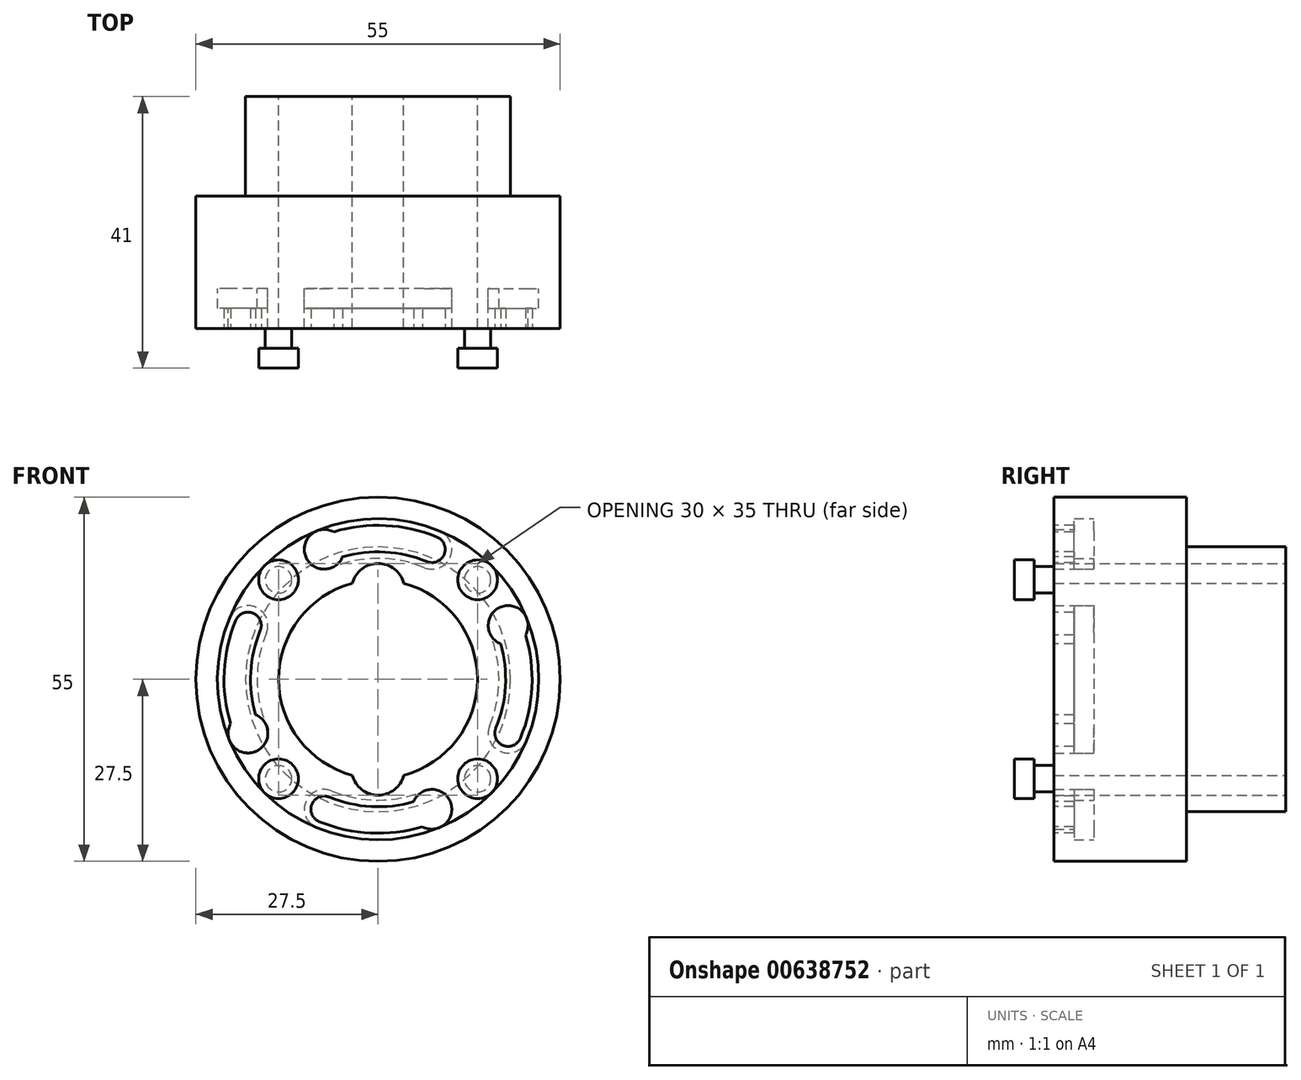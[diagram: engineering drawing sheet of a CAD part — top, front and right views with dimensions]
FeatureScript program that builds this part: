
annotation { "Feature Type Name" : "Feature", "Feature Type Description" : "" }
export const myFeature = defineFeature(function(context is Context, id is Id, definition is map)
    precondition{}
    {
        {
            var Q0;
            Q0=qCreatedBy(makeId("Front.planeOp"),FACE);
            var sketch = newSketch(context, id + "F0", { "sketchPlane" : qUnion([Q0])});
            skCircle(sketch, "E0", {"center": v(0, 0) * mm, "radius": 15 * mm});
            skCircle(sketch, "E1", {"center": v(0, 0) * mm, "radius": 20 * mm});
            skLineSegment(sketch, "E2", {"start": v(-4, 13.5) * mm, "end": v(4, 13.5) * mm});
            skArc(sketch, "E3", {"start": v(4, 13.5) * mm, "mid": v(0, 17.5) * mm, "end": v(-4, 13.5) * mm});
            skArc(sketch, "E4.MirrorCS", {"start": v(4, -13.5) * mm, "mid": v(0, -17.5) * mm, "end": v(-4, -13.5) * mm});
            skLineSegment(sketch, "E5.MirrorCS", {"start": v(-4, -13.5) * mm, "end": v(4, -13.5) * mm});
            skSolve(sketch);
        }
        {
            var Q0;
            Q0=qSketchRegion(id+"F0",true);
            extrude(context, id + "F1", {"entities" : qUnion([Q0]), "depth" : 35 * mm, "offsetDistance" : 25 * mm});
        }
        {
            var Q0;
            Q0=makeQuery(id+"F1.opExtrude","CAP_FACE",FACE,{"disambiguationData":[OSD([sQuery(id+"F0.wireOp",EDGE,"E0"),sQuery(id+"F0.wireOp",EDGE,"E1"),sQuery(id+"F0.wireOp",EDGE,"E3"),sQuery(id+"F0.wireOp",EDGE,"E4.MirrorCS")])],"isStart":false});
            var sketch = newSketch(context, id + "F2", { "sketchPlane" : qUnion([Q0])});
            skCircle(sketch, "E6", {"center": v(0, 0) * mm, "radius": 27.5 * mm});
            skCircle(sketch, "E7", {"center": v(0, 0) * mm, "radius": 20 * mm});
            skSolve(sketch);
        }
        {
            var Q0;
            Q0=qSketchRegion(id+"F2",true);
            extrude(context, id + "F3", {"entities" : qUnion([Q0]), "operationType" : NewBodyOperationType.ADD, "oppositeDirection" : true, "depth" : 20 * mm, "offsetDistance" : 25 * mm});
        }
        {
            var Q0;
            Q0=makeQuery(id+"F3.boolean.opBoolean","MERGE",FACE,{"derivedFrom":[makeQuery(id+"F1.opExtrude","CAP_FACE",FACE,{"disambiguationData":[OSD([sQuery(id+"F0.wireOp",EDGE,"E0"),sQuery(id+"F0.wireOp",EDGE,"E1"),sQuery(id+"F0.wireOp",EDGE,"E3"),sQuery(id+"F0.wireOp",EDGE,"E4.MirrorCS")])],"isStart":false}),makeQuery(id+"F3.opExtrude","CAP_FACE",FACE,{"disambiguationData":[OSD([sQuery(id+"F2.wireOp",EDGE,"E6"),sQuery(id+"F2.wireOp",EDGE,"E7")])],"isStart":true})]});
            var sketch = newSketch(context, id + "F4", { "sketchPlane" : qUnion([Q0])});
            skLineSegment(sketch, "E8", {"start": v(0, 0) * mm, "end": v(15.03, 15.03) * mm, "construction": true});
            skCircle(sketch, "E9", {"center": v(15.03, 15.03) * mm, "radius": 2 * mm});
            skLineSegment(sketch, "E10", {"start": v(0, 0) * mm, "end": v(0, 25.2) * mm, "construction": true});
            skPoint(sketch, "E10.endSnap0", {"position": v(0, 17.5) * mm});
            skCircle(sketch, "E11.1.0", {"center": v(-15.03, 15.03) * mm, "radius": 2 * mm});
            skCircle(sketch, "E11.2.0", {"center": v(-15.03, -15.03) * mm, "radius": 2 * mm});
            skCircle(sketch, "E11.3.0", {"center": v(15.03, -15.03) * mm, "radius": 2 * mm});
            skPoint(sketch, "E11.center", {"position": v(0, 0) * mm});
            skSolve(sketch);
        }
        {
            var Q0;
            Q0 = qSketchRegion(id + "F4", true);
            extrude(context, id + "F5", {"entities" : qUnion([Q0]), "operationType" : NewBodyOperationType.ADD, "depth" : 3 * mm, "offsetDistance" : 25 * mm});
        }
        {
            var Q0;
            Q0=makeQuery(id+"F5.opExtrude","CAP_FACE",FACE,{"disambiguationData":[OSD([sQuery(id+"F4.wireOp",EDGE,"E9")])],"isStart":false});
            var sketch = newSketch(context, id + "F6", { "sketchPlane" : qUnion([Q0])});
            skCircle(sketch, "E12", {"center": v(15.03, 15.03) * mm, "radius": 3 * mm});
            skCircle(sketch, "E13.1.0", {"center": v(-15.03, 15.03) * mm, "radius": 3 * mm});
            skCircle(sketch, "E13.2.0", {"center": v(-15.03, -15.03) * mm, "radius": 3 * mm});
            skCircle(sketch, "E13.3.0", {"center": v(15.03, -15.03) * mm, "radius": 3 * mm});
            skPoint(sketch, "E13.center", {"position": v(0, 0) * mm});
            skSolve(sketch);
        }
        {
            var Q0;
            Q0 = qSketchRegion(id + "F6", true);
            extrude(context, id + "F7", {"entities" : qUnion([Q0]), "operationType" : NewBodyOperationType.ADD, "depth" : 3 * mm, "offsetDistance" : 25 * mm});
        }
        {
            var Q0;
            Q0=makeQuery(id+"F3.boolean.opBoolean","MERGE",FACE,{"derivedFrom":[makeQuery(id+"F1.opExtrude","CAP_FACE",FACE,{"disambiguationData":[OSD([sQuery(id+"F0.wireOp",EDGE,"E0"),sQuery(id+"F0.wireOp",EDGE,"E1"),sQuery(id+"F0.wireOp",EDGE,"E3"),sQuery(id+"F0.wireOp",EDGE,"E4.MirrorCS")])],"isStart":false}),makeQuery(id+"F3.opExtrude","CAP_FACE",FACE,{"disambiguationData":[OSD([sQuery(id+"F2.wireOp",EDGE,"E6"),sQuery(id+"F2.wireOp",EDGE,"E7")])],"isStart":true})]});
            var sketch = newSketch(context, id + "F8", { "sketchPlane" : qUnion([Q0])});
            skLineSegment(sketch, "E14", {"start": v(0, 0) * mm, "end": v(0, 21.25) * mm, "construction": true});
            skLineSegment(sketch, "E15", {"start": v(0, 0) * mm, "end": v(-8.13, 19.63) * mm, "construction": true});
            skLineSegment(sketch, "E16.MirrorCS", {"start": v(0, 0) * mm, "end": v(8.13, 19.63) * mm, "construction": true});
            skCircle(sketch, "E17", {"center": v(-8.13, 19.63) * mm, "radius": 2 * mm});
            skCircle(sketch, "E18.MirrorC", {"center": v(8.13, 19.63) * mm, "radius": 2 * mm});
            skArc(sketch, "E19", {"start": v(-8.91, 21.47) * mm, "mid": v(-4.54, 22.8) * mm, "end": v(0, 23.25) * mm});
            skArc(sketch, "E20", {"start": v(-7.37, 17.78) * mm, "mid": v(-3.76, 18.88) * mm, "end": v(0, 19.25) * mm});
            skArc(sketch, "E21.MirrorCS", {"start": v(8.91, 21.47) * mm, "mid": v(4.54, 22.8) * mm, "end": v(0, 23.25) * mm});
            skArc(sketch, "E22.MirrorCS", {"start": v(7.37, 17.78) * mm, "mid": v(3.76, 18.88) * mm, "end": v(0, 19.25) * mm});
            skLineSegment(sketch, "E23.1.0", {"start": v(0, 0) * mm, "end": v(-21.25, 0) * mm, "construction": true});
            skArc(sketch, "E23.1.1", {"start": v(-21.47, 8.91) * mm, "mid": v(-22.8, 4.54) * mm, "end": v(-23.25, 0) * mm});
            skArc(sketch, "E23.1.2", {"start": v(-17.78, -7.37) * mm, "mid": v(-18.88, -3.76) * mm, "end": v(-19.25, 0) * mm});
            skLineSegment(sketch, "E23.1.3", {"start": v(0, 0) * mm, "end": v(-19.63, 8.13) * mm, "construction": true});
            skArc(sketch, "E23.1.4", {"start": v(-17.78, 7.37) * mm, "mid": v(-18.88, 3.76) * mm, "end": v(-19.25, 0) * mm});
            skLineSegment(sketch, "E23.1.5", {"start": v(0, 0) * mm, "end": v(-19.63, -8.13) * mm, "construction": true});
            skCircle(sketch, "E23.1.6", {"center": v(-19.63, 8.13) * mm, "radius": 2 * mm});
            skArc(sketch, "E23.1.7", {"start": v(-21.47, -8.91) * mm, "mid": v(-22.8, -4.54) * mm, "end": v(-23.25, 0) * mm});
            skCircle(sketch, "E23.1.8", {"center": v(-19.63, -8.13) * mm, "radius": 2 * mm});
            skLineSegment(sketch, "E23.2.0", {"start": v(0, 0) * mm, "end": v(0, -21.25) * mm, "construction": true});
            skArc(sketch, "E23.2.1", {"start": v(-8.91, -21.47) * mm, "mid": v(-4.54, -22.8) * mm, "end": v(0, -23.25) * mm});
            skArc(sketch, "E23.2.2", {"start": v(7.37, -17.78) * mm, "mid": v(3.76, -18.88) * mm, "end": v(0, -19.25) * mm});
            skLineSegment(sketch, "E23.2.3", {"start": v(0, 0) * mm, "end": v(-8.13, -19.63) * mm, "construction": true});
            skArc(sketch, "E23.2.4", {"start": v(-7.37, -17.78) * mm, "mid": v(-3.76, -18.88) * mm, "end": v(0, -19.25) * mm});
            skLineSegment(sketch, "E23.2.5", {"start": v(0, 0) * mm, "end": v(8.13, -19.63) * mm, "construction": true});
            skCircle(sketch, "E23.2.6", {"center": v(-8.13, -19.63) * mm, "radius": 2 * mm});
            skArc(sketch, "E23.2.7", {"start": v(8.91, -21.47) * mm, "mid": v(4.54, -22.8) * mm, "end": v(0, -23.25) * mm});
            skCircle(sketch, "E23.2.8", {"center": v(8.13, -19.63) * mm, "radius": 2 * mm});
            skLineSegment(sketch, "E23.3.0", {"start": v(0, 0) * mm, "end": v(21.25, 0) * mm, "construction": true});
            skArc(sketch, "E23.3.1", {"start": v(21.47, -8.91) * mm, "mid": v(22.8, -4.54) * mm, "end": v(23.25, 0) * mm});
            skArc(sketch, "E23.3.2", {"start": v(17.78, 7.37) * mm, "mid": v(18.88, 3.76) * mm, "end": v(19.25, 0) * mm});
            skLineSegment(sketch, "E23.3.3", {"start": v(0, 0) * mm, "end": v(19.63, -8.13) * mm, "construction": true});
            skArc(sketch, "E23.3.4", {"start": v(17.78, -7.37) * mm, "mid": v(18.88, -3.76) * mm, "end": v(19.25, 0) * mm});
            skLineSegment(sketch, "E23.3.5", {"start": v(0, 0) * mm, "end": v(19.63, 8.13) * mm, "construction": true});
            skCircle(sketch, "E23.3.6", {"center": v(19.63, -8.13) * mm, "radius": 2 * mm});
            skArc(sketch, "E23.3.7", {"start": v(21.47, 8.91) * mm, "mid": v(22.8, 4.54) * mm, "end": v(23.25, 0) * mm});
            skCircle(sketch, "E23.3.8", {"center": v(19.63, 8.13) * mm, "radius": 2 * mm});
            skSolve(sketch);
        }
        {
            var Q0;
            Q0 = qSketchRegion(id + "F8", true);
            extrude(context, id + "F9", {"entities" : qUnion([Q0]), "operationType" : NewBodyOperationType.REMOVE, "oppositeDirection" : true, "depth" : 6 * mm, "offsetDistance" : 25 * mm});
        }
        {
            var Q0;
            Q0=makeQuery(id+"F9.boolean.opBoolean","COPY",FACE,{"derivedFrom":makeQuery(id+"F9.opExtrude","CAP_FACE",FACE,{"disambiguationData":[OSD([sQuery(id+"F8.wireOp",EDGE,"E17"),sQuery(id+"F8.wireOp",EDGE,"E18.MirrorC"),sQuery(id+"F8.wireOp",EDGE,"E19"),sQuery(id+"F8.wireOp",EDGE,"E20"),sQuery(id+"F8.wireOp",EDGE,"E21.MirrorCS"),sQuery(id+"F8.wireOp",EDGE,"E22.MirrorCS")])],"isStart":false})});
            var sketch = newSketch(context, id + "F10", { "sketchPlane" : qUnion([Q0])});
            skLineSegment(sketch, "E24", {"start": v(0, 0) * mm, "end": v(0, 21.25) * mm, "construction": true});
            skLineSegment(sketch, "E25", {"start": v(0, 0) * mm, "end": v(-8.13, 19.63) * mm, "construction": true});
            skLineSegment(sketch, "E26.MirrorCS", {"start": v(0, 0) * mm, "end": v(8.13, 19.63) * mm, "construction": true});
            skCircle(sketch, "E27", {"center": v(-8.13, 19.63) * mm, "radius": 3 * mm});
            skCircle(sketch, "E28.MirrorC", {"center": v(8.13, 19.63) * mm, "radius": 3 * mm});
            skArc(sketch, "E29", {"start": v(-9.3, 22.4) * mm, "mid": v(-4.74, 23.78) * mm, "end": v(0, 24.25) * mm});
            skArc(sketch, "E30", {"start": v(-6.98, 16.86) * mm, "mid": v(-3.56, 17.9) * mm, "end": v(0, 18.25) * mm});
            skArc(sketch, "E31.MirrorCS", {"start": v(9.3, 22.4) * mm, "mid": v(4.74, 23.78) * mm, "end": v(0, 24.25) * mm});
            skArc(sketch, "E32.MirrorCS", {"start": v(6.98, 16.86) * mm, "mid": v(3.56, 17.9) * mm, "end": v(0, 18.25) * mm});
            skArc(sketch, "E33.1.0", {"start": v(-22.4, 9.3) * mm, "mid": v(-23.78, 4.74) * mm, "end": v(-24.25, 0) * mm});
            skCircle(sketch, "E33.1.1", {"center": v(-19.63, 8.13) * mm, "radius": 3 * mm});
            skArc(sketch, "E33.1.2", {"start": v(-22.4, -9.3) * mm, "mid": v(-23.78, -4.74) * mm, "end": v(-24.25, 0) * mm});
            skArc(sketch, "E33.1.3", {"start": v(-16.86, -6.98) * mm, "mid": v(-17.9, -3.56) * mm, "end": v(-18.25, 0) * mm});
            skLineSegment(sketch, "E33.1.4", {"start": v(0, 0) * mm, "end": v(-21.25, 0) * mm, "construction": true});
            skLineSegment(sketch, "E33.1.5", {"start": v(0, 0) * mm, "end": v(-19.63, -8.13) * mm, "construction": true});
            skLineSegment(sketch, "E33.1.6", {"start": v(0, 0) * mm, "end": v(-19.63, 8.13) * mm, "construction": true});
            skCircle(sketch, "E33.1.7", {"center": v(-19.63, -8.13) * mm, "radius": 3 * mm});
            skArc(sketch, "E33.1.8", {"start": v(-16.86, 6.98) * mm, "mid": v(-17.9, 3.56) * mm, "end": v(-18.25, 0) * mm});
            skArc(sketch, "E33.2.0", {"start": v(-9.3, -22.4) * mm, "mid": v(-4.74, -23.78) * mm, "end": v(0, -24.25) * mm});
            skCircle(sketch, "E33.2.1", {"center": v(-8.13, -19.63) * mm, "radius": 3 * mm});
            skArc(sketch, "E33.2.2", {"start": v(9.3, -22.4) * mm, "mid": v(4.74, -23.78) * mm, "end": v(0, -24.25) * mm});
            skArc(sketch, "E33.2.3", {"start": v(6.98, -16.86) * mm, "mid": v(3.56, -17.9) * mm, "end": v(0, -18.25) * mm});
            skLineSegment(sketch, "E33.2.4", {"start": v(0, 0) * mm, "end": v(0, -21.25) * mm, "construction": true});
            skLineSegment(sketch, "E33.2.5", {"start": v(0, 0) * mm, "end": v(8.13, -19.63) * mm, "construction": true});
            skLineSegment(sketch, "E33.2.6", {"start": v(0, 0) * mm, "end": v(-8.13, -19.63) * mm, "construction": true});
            skCircle(sketch, "E33.2.7", {"center": v(8.13, -19.63) * mm, "radius": 3 * mm});
            skArc(sketch, "E33.2.8", {"start": v(-6.98, -16.86) * mm, "mid": v(-3.56, -17.9) * mm, "end": v(0, -18.25) * mm});
            skArc(sketch, "E33.3.0", {"start": v(22.4, -9.3) * mm, "mid": v(23.78, -4.74) * mm, "end": v(24.25, 0) * mm});
            skCircle(sketch, "E33.3.1", {"center": v(19.63, -8.13) * mm, "radius": 3 * mm});
            skArc(sketch, "E33.3.2", {"start": v(22.4, 9.3) * mm, "mid": v(23.78, 4.74) * mm, "end": v(24.25, 0) * mm});
            skArc(sketch, "E33.3.3", {"start": v(16.86, 6.98) * mm, "mid": v(17.9, 3.56) * mm, "end": v(18.25, 0) * mm});
            skLineSegment(sketch, "E33.3.4", {"start": v(0, 0) * mm, "end": v(21.25, 0) * mm, "construction": true});
            skLineSegment(sketch, "E33.3.5", {"start": v(0, 0) * mm, "end": v(19.63, 8.13) * mm, "construction": true});
            skLineSegment(sketch, "E33.3.6", {"start": v(0, 0) * mm, "end": v(19.63, -8.13) * mm, "construction": true});
            skCircle(sketch, "E33.3.7", {"center": v(19.63, 8.13) * mm, "radius": 3 * mm});
            skArc(sketch, "E33.3.8", {"start": v(16.86, -6.98) * mm, "mid": v(17.9, -3.56) * mm, "end": v(18.25, 0) * mm});
            skSolve(sketch);
        }
        {
            var Q0;
            Q0 = qSketchRegion(id + "F10", true);
            extrude(context, id + "F11", {"entities" : qUnion([Q0]), "operationType" : NewBodyOperationType.REMOVE, "depth" : 3 * mm, "offsetDistance" : 25 * mm});
        }
        {
            var Q0;
            Q0=makeQuery(id+"F3.boolean.opBoolean","MERGE",FACE,{"derivedFrom":[makeQuery(id+"F1.opExtrude","CAP_FACE",FACE,{"disambiguationData":[OSD([sQuery(id+"F0.wireOp",EDGE,"E0"),sQuery(id+"F0.wireOp",EDGE,"E1"),sQuery(id+"F0.wireOp",EDGE,"E3"),sQuery(id+"F0.wireOp",EDGE,"E4.MirrorCS")])],"isStart":false}),makeQuery(id+"F3.opExtrude","CAP_FACE",FACE,{"disambiguationData":[OSD([sQuery(id+"F2.wireOp",EDGE,"E6"),sQuery(id+"F2.wireOp",EDGE,"E7")])],"isStart":true})]});
            var sketch = newSketch(context, id + "F12", { "sketchPlane" : qUnion([Q0])});
            skCircle(sketch, "E34", {"center": v(-8.13, 19.63) * mm, "radius": 3 * mm});
            skCircle(sketch, "E35.1.0", {"center": v(-19.63, -8.13) * mm, "radius": 3 * mm});
            skCircle(sketch, "E35.2.0", {"center": v(8.13, -19.63) * mm, "radius": 3 * mm});
            skCircle(sketch, "E35.3.0", {"center": v(19.63, 8.13) * mm, "radius": 3 * mm});
            skPoint(sketch, "E35.center", {"position": v(0, 0) * mm});
            skSolve(sketch);
        }
        {
            var Q0;
            Q0 = qSketchRegion(id + "F12", true);
            extrude(context, id + "F13", {"entities" : qUnion([Q0]), "operationType" : NewBodyOperationType.REMOVE, "oppositeDirection" : true, "depth" : 6 * mm, "offsetDistance" : 25 * mm});
        }
    });
